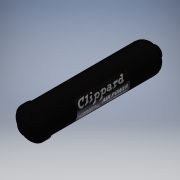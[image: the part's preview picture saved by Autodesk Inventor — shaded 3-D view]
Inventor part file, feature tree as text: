
AUTODESK INVENTOR PART (.ipt)
format: ipt  version: 2017.1 (Build 211199000, 199)  size: 204,800 bytes
history: native  units: in
note: dims shown in document units (in); Inventor stores cm internally (conversion verified against a paired STEP export)
features: sketch x8, extrude x4, revolve x3, fillet x2, other x2, projected_geometry x2, plane x1
ambient origin geometry x8: Origin, YZ Plane, XZ Plane, XY Plane, X Axis, Y Axis, Z Axis, Center Point
bodies: Solid1 (feature_tree)
feature tree (22):
  revolve  "Revolution1"  [1 undecoded]
  fillet  "Fillet1"  [1 undecoded]
  revolve  "Revolution2"  [1 undecoded]
  fillet  "Fillet2"  Radius=0.75in
  revolve  "Revolution3"  [1 undecoded]
  extrude  "Extrusion1"  Depth=0.144in TaperAngle=0.0deg
  extrude  "Extrusion2"  Depth=0.1in TaperAngle=0.0deg
  extrude  "Extrusion3"  [1 undecoded]
  extrude  "Extrusion4"  [1 undecoded]
  plane  "Work Plane1"
  other  "Decal1"
  sketch  "Sketch1"  dims[d0=1.28in d1=10.459in d2=90.0deg]
  sketch  "Sketch2"  dims[d3=0.75in d4=1.39in d5=0.75in]
  sketch  "Sketch3"  dims[d6=90.0deg d7=0.25in]
  sketch  "Sketch4"  dims[d8=90.0deg d9=0.144in d10=0.0in]
  projected_geometry  "Projected Loop1"
  sketch  "Sketch5"  dims[d11=0.322in d12=0.0in d13=0.1in d14=0.0in]
  projected_geometry  "Projected Loop2"
  sketch  "Sketch6"  dims[d15=0.1in d16=0.0in]
  sketch  "Sketch7"
  sketch  "Sketch8"
  other  "Image1"
note: 6 required parameter values undecoded (feature->parameter linkage not recoverable at this tier; creation-order binding heuristic only, values carry confidence <= 0.55)